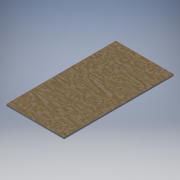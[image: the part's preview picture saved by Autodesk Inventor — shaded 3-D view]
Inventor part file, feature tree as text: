
AUTODESK INVENTOR PART (.ipt)
format: ipt  version: 2018.2 (Build 222227000, 227)  size: 110,592 bytes
history: native  units: in
note: dims shown in document units (in); Inventor stores cm internally (conversion verified against a paired STEP export)
features: extrude x1, sketch x1
ambient origin geometry x8: Origin, YZ Plane, XZ Plane, XY Plane, X Axis, Y Axis, Z Axis, Center Point
bodies: Solid1 (feature_tree)
feature tree (2):
  extrude  "Extrusion1"  Depth=0.75in
  sketch  "Sketch1"  dims[d0=28.226in d1=0.75in d2=53.463in d3=0.0in]
